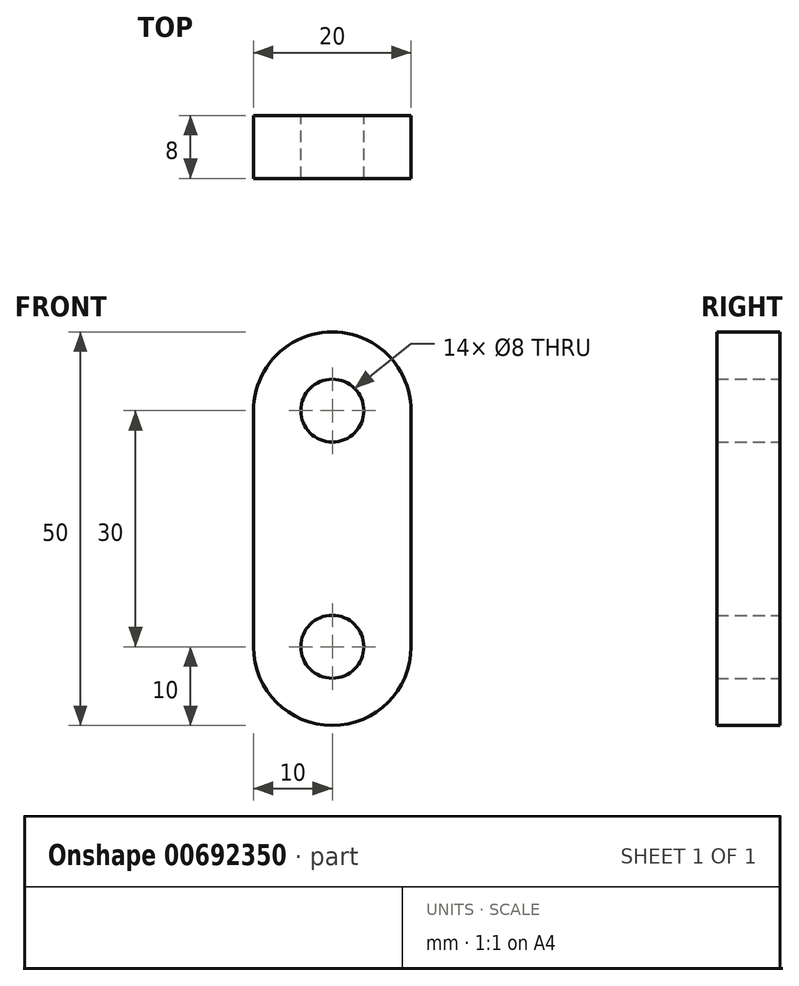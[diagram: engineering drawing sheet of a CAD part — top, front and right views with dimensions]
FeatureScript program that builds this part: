
annotation { "Feature Type Name" : "Feature", "Feature Type Description" : "" }
export const myFeature = defineFeature(function(context is Context, id is Id, definition is map)
    precondition{}
    {
        {
            var Q0;
            Q0=qCreatedBy(makeId("Front.planeOp"),FACE);
            var sketch = newSketch(context, id + "F0", { "sketchPlane" : qUnion([Q0])});
            skCircle(sketch, "E0", {"center": v(0, 0) * mm, "radius": 4 * mm});
            skArc(sketch, "E1", {"start": v(-10, 0) * mm, "mid": v(0, -10) * mm, "end": v(10, 0) * mm});
            skLineSegment(sketch, "E2", {"start": v(-10, 0) * mm, "end": v(-10, 29.91) * mm});
            skLineSegment(sketch, "E3", {"start": v(10, 0) * mm, "end": v(10, 30.09) * mm});
            skCircle(sketch, "E4", {"center": v(0, 30) * mm, "radius": 4 * mm});
            skArc(sketch, "E5", {"start": v(10, 29.91) * mm, "mid": v(0, 40) * mm, "end": v(-10, 29.91) * mm});
            skSolve(sketch);
        }
        {
            var Q0;
            Q0 = qSketchRegion(id + "F0", true);
            extrude(context, id + "F1", {"entities" : qUnion([Q0]), "depth" : 8 * mm, "offsetDistance" : 25 * mm});
        }
    });
